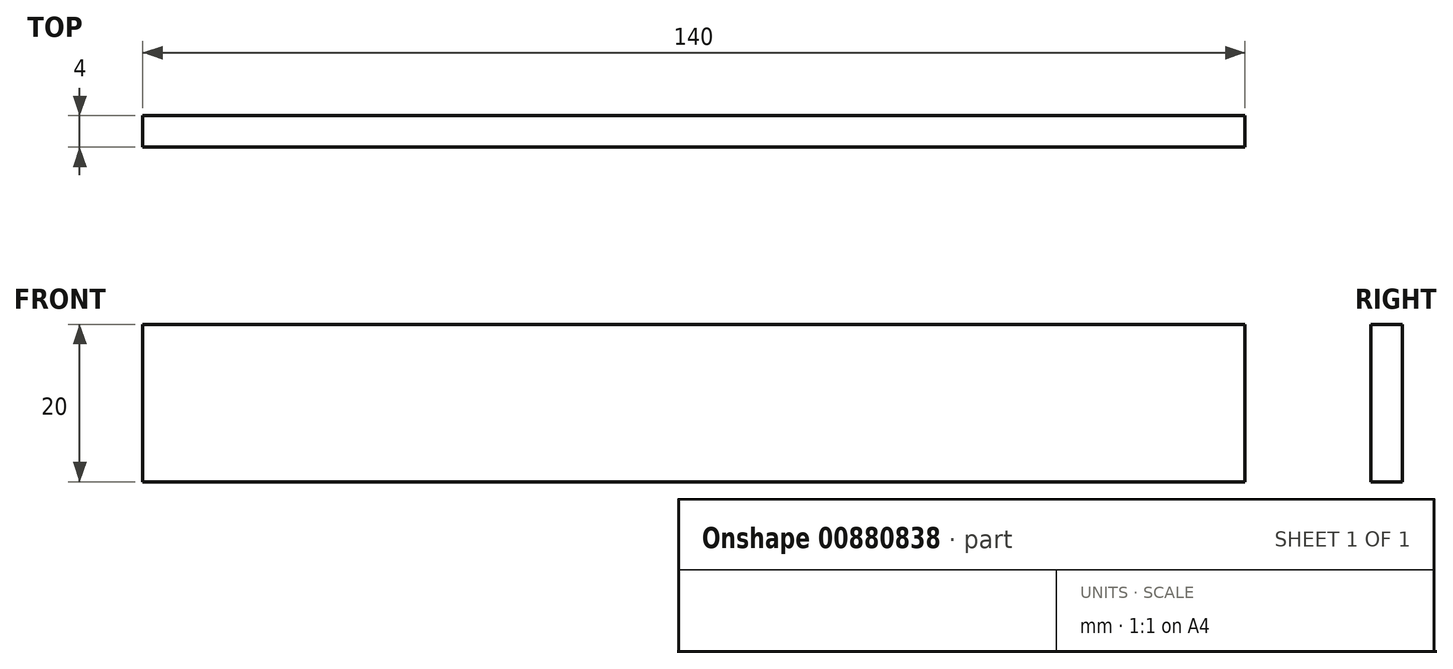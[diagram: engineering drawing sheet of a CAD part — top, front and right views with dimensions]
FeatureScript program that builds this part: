
annotation { "Feature Type Name" : "Feature", "Feature Type Description" : "" }
export const myFeature = defineFeature(function(context is Context, id is Id, definition is map)
    precondition{}
    {
        {
            var Q0;
            Q0=qCreatedBy(makeId("Front.planeOp"),FACE);
            var sketch = newSketch(context, id + "F0", { "sketchPlane" : qUnion([Q0])});
            skLineSegment(sketch, "E0.bottom", {"start": v(-61, -35.3) * mm, "end": v(79, -35.3) * mm});
            skLineSegment(sketch, "E0.top", {"start": v(-61, -15.3) * mm, "end": v(79, -15.3) * mm});
            skLineSegment(sketch, "E0.left", {"start": v(-61, -35.3) * mm, "end": v(-61, -15.3) * mm});
            skLineSegment(sketch, "E0.right", {"start": v(79, -35.3) * mm, "end": v(79, -15.3) * mm});
            skSolve(sketch);
        }
        {
            var Q0;
            Q0=makeQuery(id+"F0.imprint","IMPRINT",FACE,{"disambiguationData":[TD([[makeQuery(id+"F0.imprint","IMPRINT",EDGE,{"derivedFrom":sQuery(id+"F0.wireOp",EDGE,"E0.bottom")}),1.0]])]});
            extrude(context, id + "F1", {"entities" : qUnion([Q0]), "oppositeDirection" : true, "depth" : 4 * mm, "offsetDistance" : 25.4 * mm});
        }
    });
